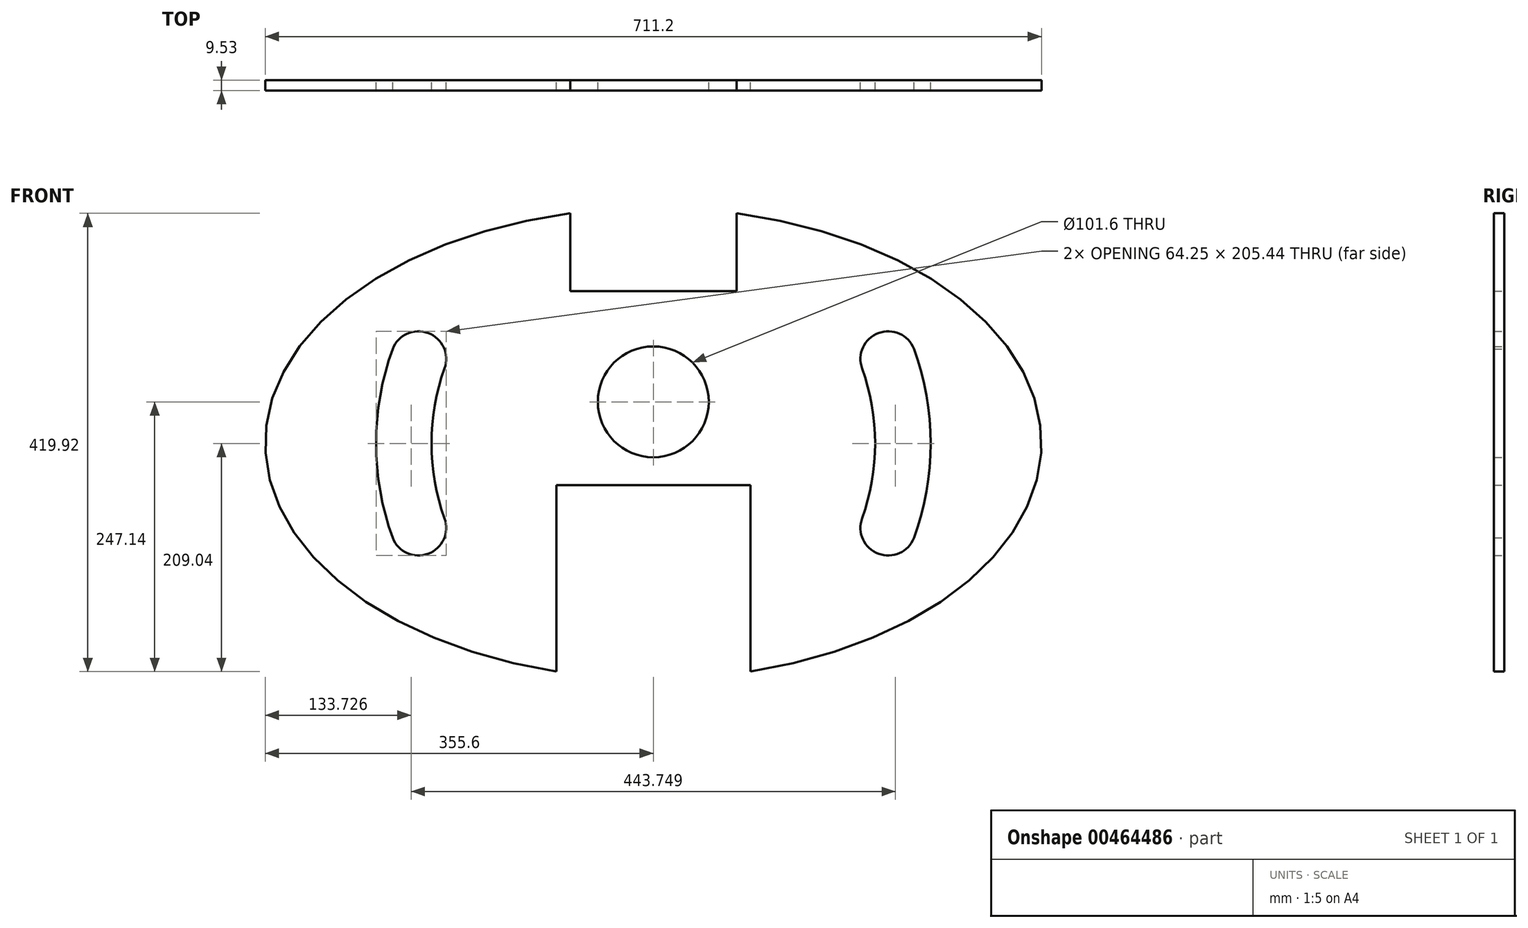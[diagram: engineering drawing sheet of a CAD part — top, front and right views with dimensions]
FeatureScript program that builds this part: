
annotation { "Feature Type Name" : "Feature", "Feature Type Description" : "" }
export const myFeature = defineFeature(function(context is Context, id is Id, definition is map)
    precondition{}
    {
        {
            var Q0;
            Q0=qCreatedBy(makeId("Front.planeOp"),FACE);
            var sketch = newSketch(context, id + "F0", { "sketchPlane" : qUnion([Q0])});
            skLineSegment(sketch, "E0", {"start": v(0, 0) * mm, "end": v(355.6, 0) * mm, "construction": true});
            skLineSegment(sketch, "E1", {"start": v(0, 0) * mm, "end": v(0, 215.9) * mm, "construction": true});
            skEllipticalArc(sketch, "E2", {});
            skLineSegment(sketch, "E3.bottom", {"start": v(76.2, 139.7) * mm, "end": v(-76.2, 139.7) * mm});
            skLineSegment(sketch, "E3.left", {"start": v(76.2, 139.7) * mm, "end": v(76.2, 210.88) * mm});
            skLineSegment(sketch, "E3.right", {"start": v(-76.2, 139.7) * mm, "end": v(-76.2, 210.88) * mm});
            skPoint(sketch, "E3.middle", {"position": v(0, 215.9) * mm});
            skLineSegment(sketch, "E4.bottom", {"start": v(88.9, -38.1) * mm, "end": v(-88.9, -38.1) * mm});
            skLineSegment(sketch, "E4.left", {"start": v(88.9, -38.1) * mm, "end": v(88.9, -209.04) * mm});
            skLineSegment(sketch, "E4.right", {"start": v(-88.9, -38.1) * mm, "end": v(-88.9, -209.04) * mm});
            skPoint(sketch, "E4.middle", {"position": v(0, -215.9) * mm});
            skLineSegment(sketch, "E5", {"start": v(0, -38.1) * mm, "end": v(0, 38.1) * mm, "construction": true});
            skCircle(sketch, "E6", {"center": v(0, 38.1) * mm, "radius": 50.8 * mm});
            skPoint(sketch, "E7.startSnap0", {"position": v(0, 107.95) * mm});
            skPoint(sketch, "E3.top.end.orphan", {"position": v(-76.2, 292.1) * mm});
            skPoint(sketch, "E3.top.start.orphan", {"position": v(76.2, 292.1) * mm});
            skPoint(sketch, "E4.top.end.orphan", {"position": v(-88.9, -393.7) * mm});
            skPoint(sketch, "E4.top.start.orphan", {"position": v(88.9, -393.7) * mm});
            skEllipticalArc(sketch, "E8.trimOffspring", {});
            skArc(sketch, "E9", {"start": v(-238.78, 86.6) * mm, "mid": v(-254, 0) * mm, "end": v(-238.78, -86.6) * mm});
            skArc(sketch, "E10", {"start": v(-191.22, 68.74) * mm, "mid": v(-203.2, 0) * mm, "end": v(-191.22, -68.74) * mm});
            skArc(sketch, "E11.trimOffspring", {"start": v(191.22, -68.74) * mm, "mid": v(203.2, 0) * mm, "end": v(191.22, 68.74) * mm});
            skArc(sketch, "E12.trimOffspring", {"start": v(238.78, -86.6) * mm, "mid": v(254, 0) * mm, "end": v(238.78, 86.6) * mm});
            skArc(sketch, "E13", {"start": v(238.78, 86.6) * mm, "mid": v(206.2, 101.11) * mm, "end": v(191.22, 68.74) * mm});
            skArc(sketch, "E14.MirrorCS", {"start": v(238.78, -86.6) * mm, "mid": v(206.2, -101.11) * mm, "end": v(191.22, -68.74) * mm});
            skArc(sketch, "E15.MirrorCS", {"start": v(-238.78, 86.6) * mm, "mid": v(-206.2, 101.11) * mm, "end": v(-191.22, 68.74) * mm});
            skArc(sketch, "E16.MirrorCS", {"start": v(-238.78, -86.6) * mm, "mid": v(-206.2, -101.11) * mm, "end": v(-191.22, -68.74) * mm});
            skPoint(sketch, "E17.orphan", {"position": v(186.97, 79.57) * mm});
            skPoint(sketch, "E18.orphan", {"position": v(233.71, 99.47) * mm});
            skPoint(sketch, "E19.MirrorCS.end.orphan", {"position": v(186.97, -79.57) * mm});
            skPoint(sketch, "E20.orphan", {"position": v(233.71, -99.47) * mm});
            skPoint(sketch, "E21.MirrorCS.start.orphan", {"position": v(-233.71, 99.47) * mm});
            skPoint(sketch, "E22.orphan", {"position": v(-186.97, 79.57) * mm});
            skPoint(sketch, "E23.MirrorCS.end.orphan", {"position": v(-186.97, -79.57) * mm});
            skPoint(sketch, "E24.orphan", {"position": v(-233.71, -99.47) * mm});
            const initialGuessF0  = {"E2": [0, 0, 0, 1, 0.2159, 0.3556, 0.21596049868495637, 2.888912398447715], "E8.trimOffspring": [0, 0, 0, 1, 0.2159, 0.3556, 3.394272908731872, 6.067224808494631]};
            skSetInitialGuess(sketch, initialGuessF0);
            skSolve(sketch);
        }
        {
            var Q0;
            Q0=makeQuery(id+"F0.imprint","IMPRINT",FACE,{"disambiguationData":[TD([[makeQuery(id+"F0.imprint","IMPRINT",EDGE,{"derivedFrom":sQuery(id+"F0.wireOp",EDGE,"E2")}),1.0]])]});
            extrude(context, id + "F1", {"entities" : qUnion([Q0]), "depth" : 9.52 * mm});
        }
    });
